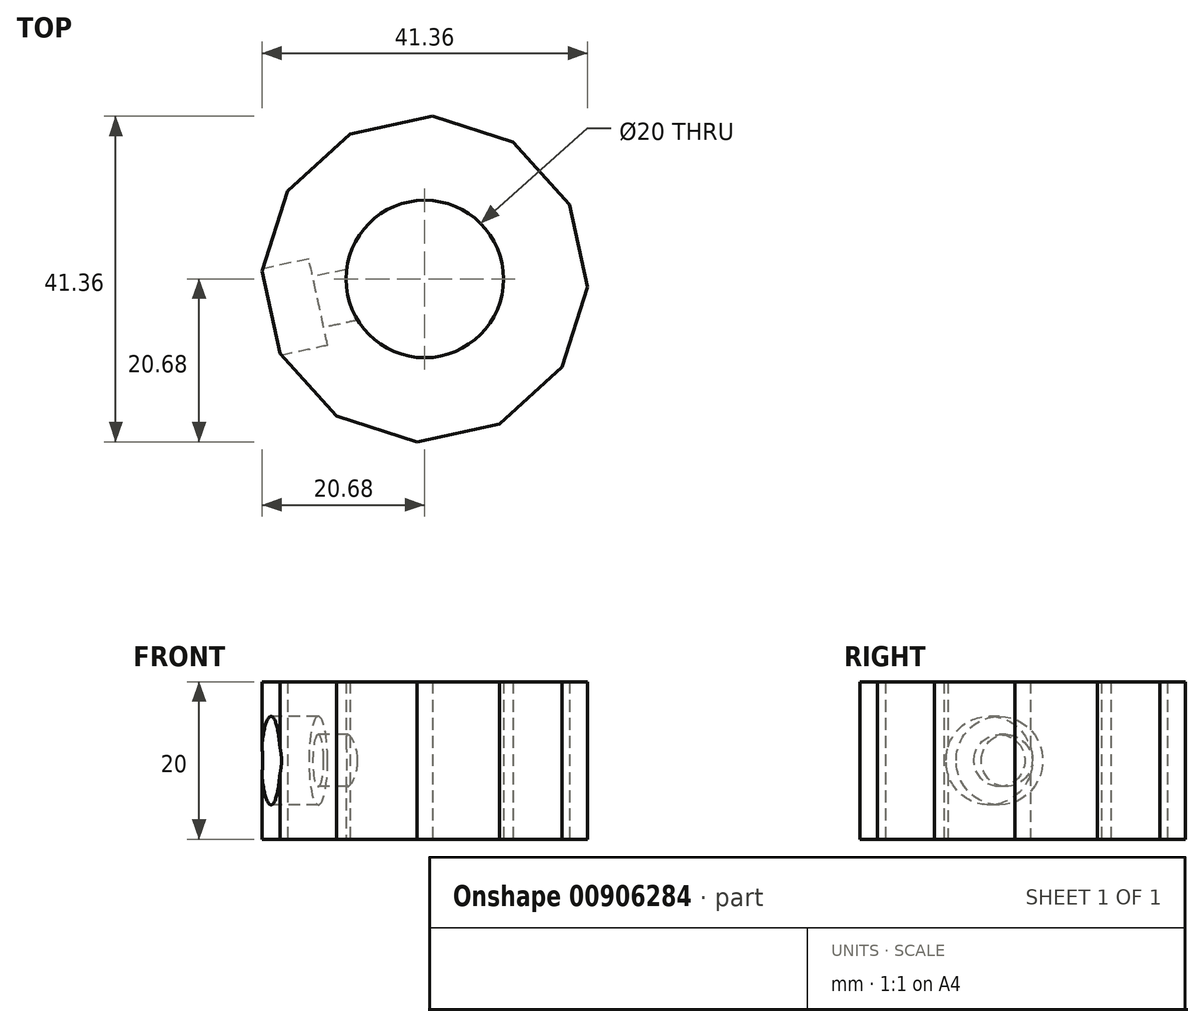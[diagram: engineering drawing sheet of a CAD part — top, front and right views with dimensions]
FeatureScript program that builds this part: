
annotation { "Feature Type Name" : "Feature", "Feature Type Description" : "" }
export const myFeature = defineFeature(function(context is Context, id is Id, definition is map)
    precondition{}
    {
        {
            var Q0;
            Q0=qCreatedBy(makeId("Top.planeOp"),FACE);
            var sketch = newSketch(context, id + "F0", { "sketchPlane" : qUnion([Q0])});
            skCircle(sketch, "E0", {"center": v(0, 0) * mm, "radius": 10 * mm});
            skCircle(sketch, "E1", {"center": v(0, 0) * mm, "radius": 20 * mm});
            skCircle(sketch, "E2.cCircle", {"center": v(0, 0) * mm, "radius": 20 * mm, "construction": true});
            skLineSegment(sketch, "E2.0", {"start": v(1, 20.68) * mm, "end": v(11.2, 17.41) * mm});
            skLineSegment(sketch, "E2.1", {"start": v(11.2, 17.41) * mm, "end": v(18.4, 9.48) * mm});
            skLineSegment(sketch, "E2.2", {"start": v(18.4, 9.48) * mm, "end": v(20.68, -1) * mm});
            skLineSegment(sketch, "E2.3", {"start": v(20.68, -1) * mm, "end": v(17.41, -11.2) * mm});
            skLineSegment(sketch, "E2.4", {"start": v(17.41, -11.2) * mm, "end": v(9.48, -18.4) * mm});
            skLineSegment(sketch, "E2.5", {"start": v(9.48, -18.4) * mm, "end": v(-1, -20.68) * mm});
            skLineSegment(sketch, "E2.6", {"start": v(-1, -20.68) * mm, "end": v(-11.2, -17.41) * mm});
            skLineSegment(sketch, "E2.7", {"start": v(-11.2, -17.41) * mm, "end": v(-18.4, -9.48) * mm});
            skLineSegment(sketch, "E2.8", {"start": v(-18.4, -9.48) * mm, "end": v(-20.68, 1) * mm});
            skLineSegment(sketch, "E2.9", {"start": v(-20.68, 1) * mm, "end": v(-17.41, 11.2) * mm});
            skLineSegment(sketch, "E2.10", {"start": v(-17.41, 11.2) * mm, "end": v(-9.48, 18.4) * mm});
            skLineSegment(sketch, "E2.11", {"start": v(-9.48, 18.4) * mm, "end": v(1, 20.68) * mm});
            skPoint(sketch, "E2.0.midPoint", {"position": v(6.1, 19.05) * mm});
            skSolve(sketch);
        }
        {
            var Q0;
            {var subQ0=sQuery(id+"F0.wireOp",EDGE,"E2.11");var subQ1=sQuery(id+"F0.wireOp",EDGE,"E1");var subQ2=makeQuery(id+"F0.imprint","INTERSECT",VERTEX,{"derivedFrom":[subQ1,subQ0]});Q0=makeQuery(id+"F0.imprint","IMPRINT",FACE,{"disambiguationData":[TD([[makeQuery(id+"F0.imprint","IMPRINT",EDGE,{"disambiguationData":[TD([[subQ2,-1.0]])],"derivedFrom":subQ1}),-1.0]])]});}
            var Q1;
            {var subQ0=sQuery(id+"F0.wireOp",EDGE,"E2.0");var subQ1=sQuery(id+"F0.wireOp",EDGE,"E1");var subQ2=makeQuery(id+"F0.imprint","INTERSECT",VERTEX,{"derivedFrom":[subQ1,subQ0]});Q1=makeQuery(id+"F0.imprint","IMPRINT",FACE,{"disambiguationData":[TD([[makeQuery(id+"F0.imprint","IMPRINT",EDGE,{"disambiguationData":[TD([[subQ2,-1.0]])],"derivedFrom":subQ1}),-1.0]])]});}
            var Q2;
            {var subQ0=sQuery(id+"F0.wireOp",EDGE,"E2.1");var subQ1=sQuery(id+"F0.wireOp",EDGE,"E1");var subQ2=makeQuery(id+"F0.imprint","INTERSECT",VERTEX,{"derivedFrom":[subQ1,subQ0]});Q2=makeQuery(id+"F0.imprint","IMPRINT",FACE,{"disambiguationData":[TD([[makeQuery(id+"F0.imprint","IMPRINT",EDGE,{"disambiguationData":[TD([[subQ2,-1.0]])],"derivedFrom":subQ1}),-1.0]])]});}
            var Q3;
            {var subQ0=sQuery(id+"F0.wireOp",EDGE,"E2.1");var subQ1=sQuery(id+"F0.wireOp",EDGE,"E1");var subQ2=makeQuery(id+"F0.imprint","INTERSECT",VERTEX,{"derivedFrom":[subQ1,subQ0]});Q3=makeQuery(id+"F0.imprint","IMPRINT",FACE,{"disambiguationData":[TD([[makeQuery(id+"F0.imprint","IMPRINT",EDGE,{"disambiguationData":[TD([[subQ2,1.0]])],"derivedFrom":subQ1}),-1.0]])]});}
            var Q4;
            {var subQ0=sQuery(id+"F0.wireOp",EDGE,"E2.2");var subQ1=sQuery(id+"F0.wireOp",EDGE,"E1");var subQ2=makeQuery(id+"F0.imprint","INTERSECT",VERTEX,{"derivedFrom":[subQ1,subQ0]});Q4=makeQuery(id+"F0.imprint","IMPRINT",FACE,{"disambiguationData":[TD([[makeQuery(id+"F0.imprint","IMPRINT",EDGE,{"disambiguationData":[TD([[subQ2,1.0]])],"derivedFrom":subQ1}),-1.0]])]});}
            var Q5;
            {var subQ0=sQuery(id+"F0.wireOp",EDGE,"E2.4");var subQ1=sQuery(id+"F0.wireOp",EDGE,"E1");var subQ2=makeQuery(id+"F0.imprint","INTERSECT",VERTEX,{"derivedFrom":[subQ1,subQ0]});Q5=makeQuery(id+"F0.imprint","IMPRINT",FACE,{"disambiguationData":[TD([[makeQuery(id+"F0.imprint","IMPRINT",EDGE,{"disambiguationData":[TD([[subQ2,-1.0]])],"derivedFrom":subQ1}),-1.0]])]});}
            var Q6;
            {var subQ0=sQuery(id+"F0.wireOp",EDGE,"E2.5");var subQ1=sQuery(id+"F0.wireOp",EDGE,"E1");var subQ2=makeQuery(id+"F0.imprint","INTERSECT",VERTEX,{"derivedFrom":[subQ1,subQ0]});Q6=makeQuery(id+"F0.imprint","IMPRINT",FACE,{"disambiguationData":[TD([[makeQuery(id+"F0.imprint","IMPRINT",EDGE,{"disambiguationData":[TD([[subQ2,-1.0]])],"derivedFrom":subQ1}),-1.0]])]});}
            var Q7;
            {var subQ0=sQuery(id+"F0.wireOp",EDGE,"E2.6");var subQ1=sQuery(id+"F0.wireOp",EDGE,"E1");var subQ2=makeQuery(id+"F0.imprint","INTERSECT",VERTEX,{"derivedFrom":[subQ1,subQ0]});Q7=makeQuery(id+"F0.imprint","IMPRINT",FACE,{"disambiguationData":[TD([[makeQuery(id+"F0.imprint","IMPRINT",EDGE,{"disambiguationData":[TD([[subQ2,-1.0]])],"derivedFrom":subQ1}),-1.0]])]});}
            var Q8;
            {var subQ0=sQuery(id+"F0.wireOp",EDGE,"E2.7");var subQ1=sQuery(id+"F0.wireOp",EDGE,"E1");var subQ2=makeQuery(id+"F0.imprint","INTERSECT",VERTEX,{"derivedFrom":[subQ1,subQ0]});Q8=makeQuery(id+"F0.imprint","IMPRINT",FACE,{"disambiguationData":[TD([[makeQuery(id+"F0.imprint","IMPRINT",EDGE,{"disambiguationData":[TD([[subQ2,-1.0]])],"derivedFrom":subQ1}),-1.0]])]});}
            var Q9;
            {var subQ0=sQuery(id+"F0.wireOp",EDGE,"E2.8");var subQ1=sQuery(id+"F0.wireOp",EDGE,"E1");var subQ2=makeQuery(id+"F0.imprint","INTERSECT",VERTEX,{"derivedFrom":[subQ1,subQ0]});Q9=makeQuery(id+"F0.imprint","IMPRINT",FACE,{"disambiguationData":[TD([[makeQuery(id+"F0.imprint","IMPRINT",EDGE,{"disambiguationData":[TD([[subQ2,-1.0]])],"derivedFrom":subQ1}),-1.0]])]});}
            var Q10;
            {var subQ0=sQuery(id+"F0.wireOp",EDGE,"E2.9");var subQ1=sQuery(id+"F0.wireOp",EDGE,"E1");var subQ2=makeQuery(id+"F0.imprint","INTERSECT",VERTEX,{"derivedFrom":[subQ1,subQ0]});Q10=makeQuery(id+"F0.imprint","IMPRINT",FACE,{"disambiguationData":[TD([[makeQuery(id+"F0.imprint","IMPRINT",EDGE,{"disambiguationData":[TD([[subQ2,-1.0]])],"derivedFrom":subQ1}),-1.0]])]});}
            var Q11;
            {var subQ0=sQuery(id+"F0.wireOp",EDGE,"E2.10");var subQ1=sQuery(id+"F0.wireOp",EDGE,"E1");var subQ2=makeQuery(id+"F0.imprint","INTERSECT",VERTEX,{"derivedFrom":[subQ1,subQ0]});Q11=makeQuery(id+"F0.imprint","IMPRINT",FACE,{"disambiguationData":[TD([[makeQuery(id+"F0.imprint","IMPRINT",EDGE,{"disambiguationData":[TD([[subQ2,-1.0]])],"derivedFrom":subQ1}),-1.0]])]});}
            var Q12;
            Q12=makeQuery(id+"F0.imprint","IMPRINT",FACE,{"disambiguationData":[TD([[makeQuery(id+"F0.imprint","IMPRINT",EDGE,{"derivedFrom":sQuery(id+"F0.wireOp",EDGE,"E0")}),-1.0]])]});
            extrude(context, id + "F1", {"entities" : qUnion([Q0, Q1, Q2, Q3, Q4, Q5, Q6, Q7, Q8, Q9, Q10, Q11, Q12]), "depth" : 20 * mm, "offsetDistance" : 25 * mm});
        }
        {
            var Q0;
            Q0=makeQuery(id+"F1.opExtrude","SWEPT_FACE",FACE,{"disambiguationData":[OSD([sQuery(id+"F0.wireOp",EDGE,"E2.8")])]});
            var sketch = newSketch(context, id + "F2", { "sketchPlane" : qUnion([Q0])});
            skPoint(sketch, "E3", {"position": v(0, 10) * mm});
            skSolve(sketch);
        }
        {
            var Q0;
            Q0=sQuery(id+"F2.wireOp",VERTEX,"E3");
            var Q1;
            Q1=makeQuery(id+"F1.opExtrude","SWEPT_BODY",BODY,{"disambiguationData":[OSD([sQuery(id+"F0.wireOp",EDGE,"E0"),sQuery(id+"F0.wireOp",EDGE,"E2.0"),sQuery(id+"F0.wireOp",EDGE,"E2.1"),sQuery(id+"F0.wireOp",EDGE,"E2.2"),sQuery(id+"F0.wireOp",EDGE,"E2.3"),sQuery(id+"F0.wireOp",EDGE,"E2.4"),sQuery(id+"F0.wireOp",EDGE,"E2.5"),sQuery(id+"F0.wireOp",EDGE,"E2.6"),sQuery(id+"F0.wireOp",EDGE,"E2.7"),sQuery(id+"F0.wireOp",EDGE,"E2.8"),sQuery(id+"F0.wireOp",EDGE,"E2.9"),sQuery(id+"F0.wireOp",EDGE,"E2.10"),sQuery(id+"F0.wireOp",EDGE,"E2.11")])]});
            hole(context, id + "F3", {"style" : HoleStyle.C_BORE, "endStyle" : HoleEndStyle.BLIND, "standardTappedOrClearance" : lookupTablePath({ "fit" : "Normal", "standard" : "ISO", "size" : "M6", "type" : "Clearance" }), "standardBlindInLast" : lookupTablePath({ "fit" : "Normal", "standard" : "ISO", "size" : "M6", "type" : "Clearance" }), "holeDiameter" : 6.6 * mm, "cBoreDiameter" : 11.25 * mm, "cBoreDepth" : 6 * mm, "majorDiameter" : 5 * mm, "holeDepth" : 20 * mm, "isTappedThrough" : true, "tappedDepth" : 12 * mm, "tapClearance" : 3, "locations" : qUnion([Q0]), "scope" : qUnion([Q1])});
        }
    });
